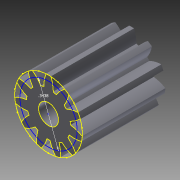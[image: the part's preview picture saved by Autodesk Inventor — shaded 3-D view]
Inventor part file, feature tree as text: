
AUTODESK INVENTOR PART (.ipt)
format: ipt  version: 2012 (Build 160160000, 160)  size: 234,496 bytes
history: native  units: in
note: dims shown in document units (in); Inventor stores cm internally (conversion verified against a paired STEP export)
features: sketch x6, other x5, plane x3
ambient origin geometry x8: Origin, YZ Plane, XZ Plane, XY Plane, X Axis, Y Axis, Z Axis, Center Point
bodies: Solid1 (feature_tree)
feature tree (14):
  other  "Spur Gear1"
  other  "Solid1::Spur Gear1"
  sketch  "Sketch1"  dims[d0=0.3937in]
  sketch  "Sketch2"
  sketch  "Sketch3"
  sketch  "Sketch4"
  sketch  "Sketch5"
  sketch  "Sketch6"
  plane  "Work Plane1"
  plane  "Work Plane2"
  plane  "Work Plane3"
  other  "Srf1::Spur Gear1"
  other  "Srf1"
  other  "TaggingFeature1"
